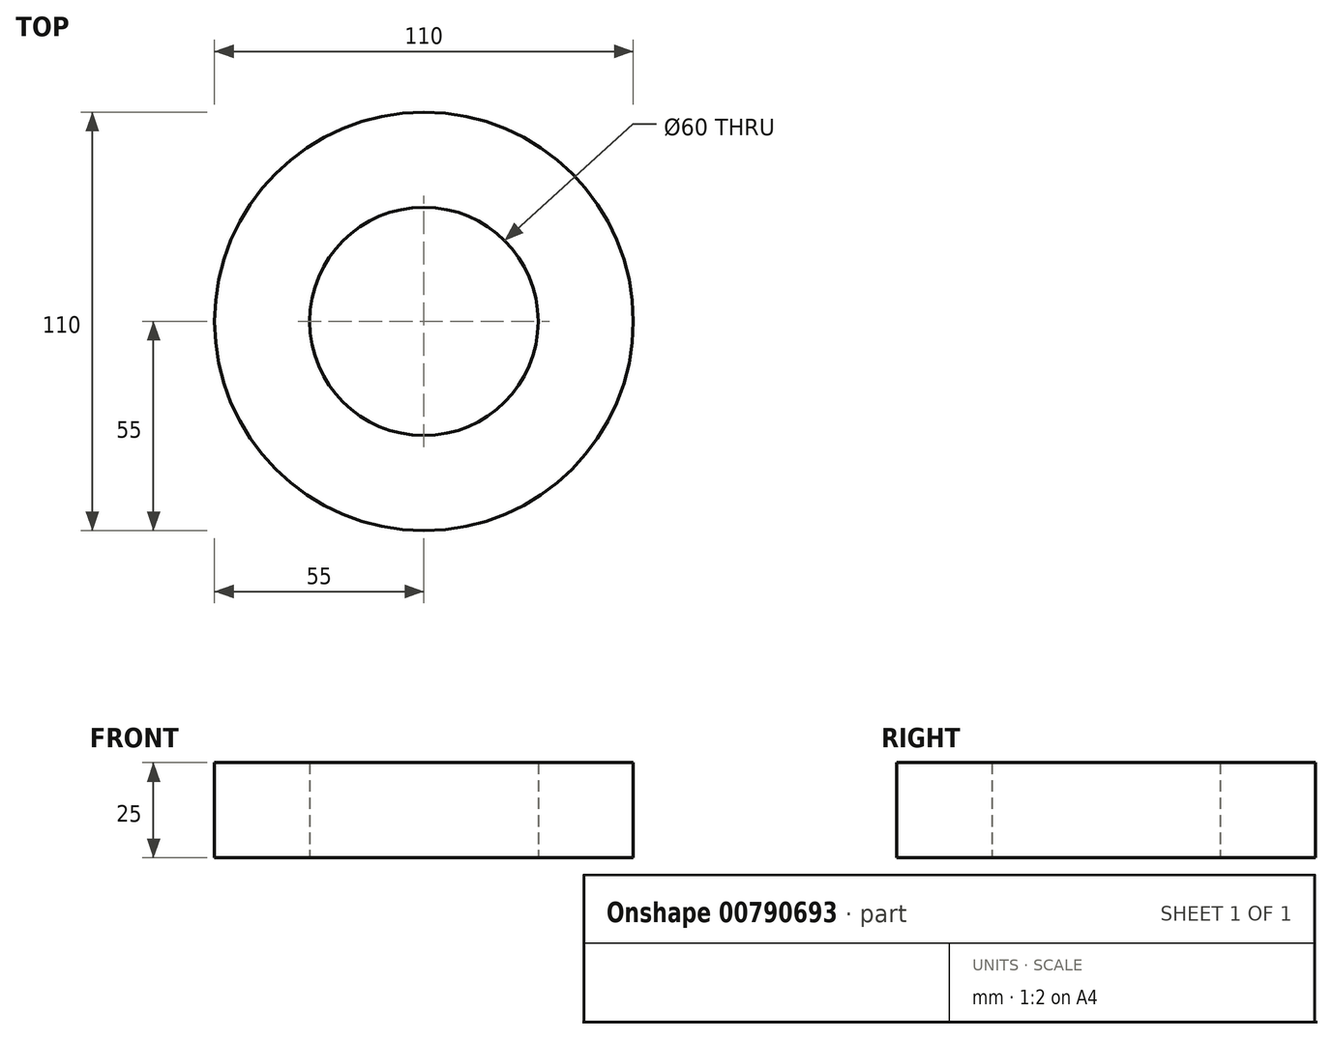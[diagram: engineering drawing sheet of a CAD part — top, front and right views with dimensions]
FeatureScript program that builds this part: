
annotation { "Feature Type Name" : "Feature", "Feature Type Description" : "" }
export const myFeature = defineFeature(function(context is Context, id is Id, definition is map)
    precondition{}
    {
        {
            var Q0;
            Q0=qCreatedBy(makeId("Top.planeOp"),FACE);
            var sketch = newSketch(context, id + "F0", { "sketchPlane" : qUnion([Q0])});
            skCircle(sketch, "E0", {"center": v(0, 0) * mm, "radius": 55 * mm});
            skCircle(sketch, "E1", {"center": v(0, 0) * mm, "radius": 30 * mm});
            skSolve(sketch);
        }
        {
            var Q0;
            Q0=makeQuery(id+"F0.imprint","IMPRINT",FACE,{"disambiguationData":[TD([[makeQuery(id+"F0.imprint","IMPRINT",EDGE,{"derivedFrom":sQuery(id+"F0.wireOp",EDGE,"E0")}),1.0]])]});
            extrude(context, id + "F1", {"entities" : qUnion([Q0]), "depth" : 25 * mm, "offsetDistance" : 25 * mm});
        }
    });
